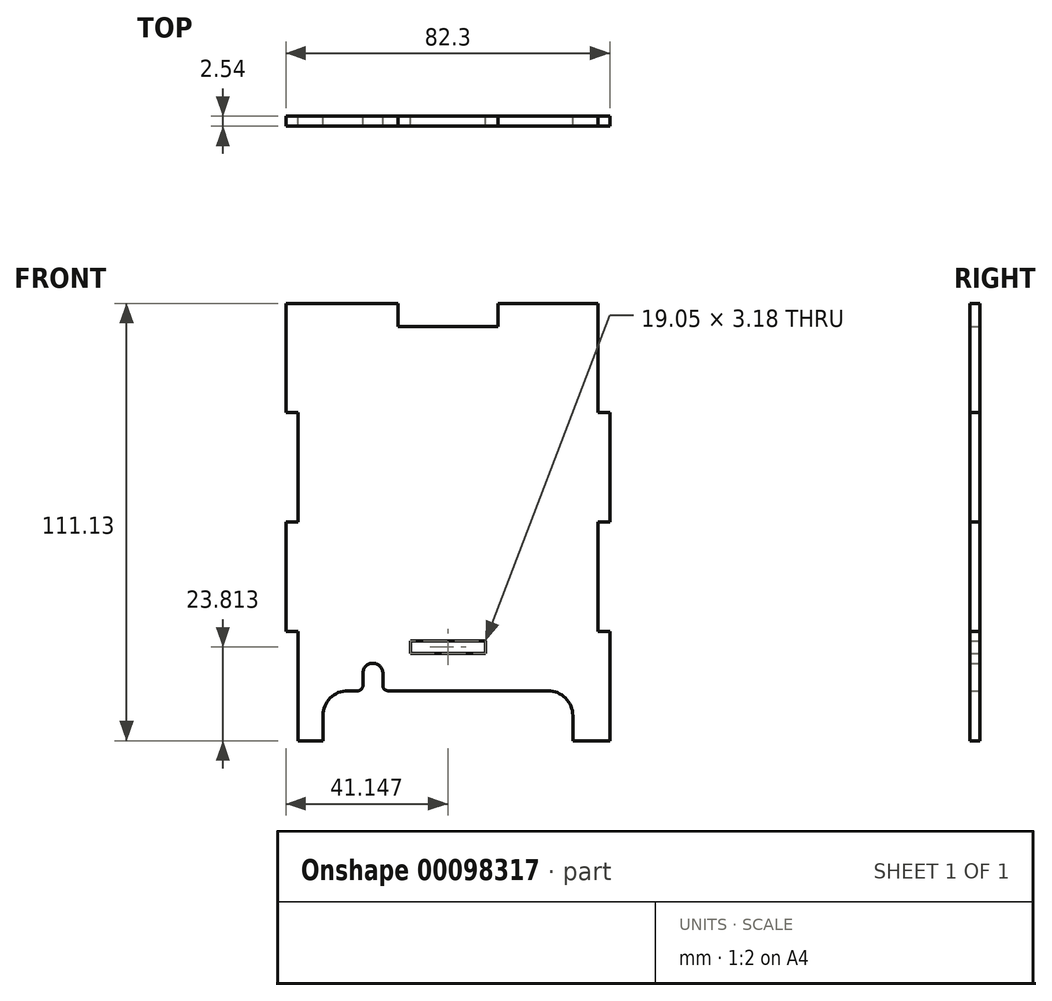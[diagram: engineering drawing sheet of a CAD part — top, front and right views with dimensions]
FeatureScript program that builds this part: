
annotation { "Feature Type Name" : "Feature", "Feature Type Description" : "" }
export const myFeature = defineFeature(function(context is Context, id is Id, definition is map)
    precondition{}
    {
        {
            var Q0;
            Q0=qCreatedBy(makeId("Front.planeOp"),FACE);
            var sketch = newSketch(context, id + "F0", { "sketchPlane" : qUnion([Q0])});
            skLineSegment(sketch, "E0", {"start": v(3.72, 63.77) * mm, "end": v(-8.98, 63.77) * mm});
            skLineSegment(sketch, "E1", {"start": v(-8.98, 63.77) * mm, "end": v(-8.98, 69.62) * mm});
            skLineSegment(sketch, "E2", {"start": v(-8.98, 69.62) * mm, "end": v(-37.43, 69.62) * mm});
            skLineSegment(sketch, "E3", {"start": v(-37.43, 69.62) * mm, "end": v(-37.43, 41.83) * mm});
            skLineSegment(sketch, "E4", {"start": v(-37.43, 41.83) * mm, "end": v(-34.38, 41.83) * mm});
            skLineSegment(sketch, "E5", {"start": v(-34.38, 41.83) * mm, "end": v(-34.38, 14.05) * mm});
            skLineSegment(sketch, "E6", {"start": v(-34.38, 14.05) * mm, "end": v(-37.43, 14.05) * mm});
            skLineSegment(sketch, "E7", {"start": v(-37.43, 14.05) * mm, "end": v(-37.43, -13.73) * mm});
            skLineSegment(sketch, "E8", {"start": v(-37.43, -13.73) * mm, "end": v(-34.38, -13.73) * mm});
            skLineSegment(sketch, "E9", {"start": v(-34.38, -13.73) * mm, "end": v(-34.38, -41.5) * mm});
            skLineSegment(sketch, "E10", {"start": v(-34.38, -41.5) * mm, "end": v(-28.03, -41.5) * mm});
            skLineSegment(sketch, "E11", {"start": v(-28.03, -41.5) * mm, "end": v(-28.03, -35.16) * mm});
            skLineSegment(sketch, "E12", {"start": v(-21.68, -28.8) * mm, "end": v(-19.14, -28.8) * mm});
            skLineSegment(sketch, "E13", {"start": v(35.47, -35.16) * mm, "end": v(35.47, -41.5) * mm});
            skLineSegment(sketch, "E14", {"start": v(35.47, -41.5) * mm, "end": v(44.87, -41.5) * mm});
            skLineSegment(sketch, "E15", {"start": v(44.87, -41.5) * mm, "end": v(44.87, -13.73) * mm});
            skLineSegment(sketch, "E16", {"start": v(44.87, -13.73) * mm, "end": v(41.82, -13.73) * mm});
            skLineSegment(sketch, "E17", {"start": v(41.82, -13.73) * mm, "end": v(41.82, 14.05) * mm});
            skLineSegment(sketch, "E18", {"start": v(41.82, 14.05) * mm, "end": v(44.87, 14.05) * mm});
            skLineSegment(sketch, "E19", {"start": v(44.87, 14.05) * mm, "end": v(44.87, 41.83) * mm});
            skLineSegment(sketch, "E20", {"start": v(44.87, 41.83) * mm, "end": v(41.82, 41.83) * mm});
            skLineSegment(sketch, "E21", {"start": v(41.82, 41.83) * mm, "end": v(41.82, 69.62) * mm});
            skLineSegment(sketch, "E22", {"start": v(41.82, 69.62) * mm, "end": v(16.42, 69.62) * mm});
            skLineSegment(sketch, "E23", {"start": v(16.42, 69.62) * mm, "end": v(16.42, 63.77) * mm});
            skLineSegment(sketch, "E24", {"start": v(16.42, 63.77) * mm, "end": v(3.72, 63.77) * mm});
            skPoint(sketch, "E25.visualSharp", {"position": v(-28.03, -28.8) * mm});
            skArc(sketch, "E25.filletArc", {"start": v(-21.68, -28.8) * mm, "mid": v(-26.17, -30.67) * mm, "end": v(-28.03, -35.16) * mm});
            skPoint(sketch, "E26.visualSharp", {"position": v(35.47, -28.8) * mm});
            skArc(sketch, "E26.filletArc", {"start": v(35.47, -35.16) * mm, "mid": v(33.6, -30.67) * mm, "end": v(29.12, -28.8) * mm});
            skLineSegment(sketch, "E27.bottom", {"start": v(-5.8, -16.1) * mm, "end": v(13.24, -16.1) * mm});
            skLineSegment(sketch, "E27.top", {"start": v(-5.8, -19.28) * mm, "end": v(13.24, -19.28) * mm});
            skLineSegment(sketch, "E27.left", {"start": v(-5.8, -16.1) * mm, "end": v(-5.8, -19.28) * mm});
            skLineSegment(sketch, "E27.right", {"start": v(13.24, -16.1) * mm, "end": v(13.24, -19.28) * mm});
            skLineSegment(sketch, "E28.left", {"start": v(-17.87, -27.54) * mm, "end": v(-17.87, -24.36) * mm});
            skLineSegment(sketch, "E28.right", {"start": v(-12.8, -27.54) * mm, "end": v(-12.8, -24.36) * mm});
            skArc(sketch, "E29", {"start": v(-12.8, -24.36) * mm, "mid": v(-15.33, -21.82) * mm, "end": v(-17.87, -24.36) * mm});
            skLineSegment(sketch, "E30.trimOffspring", {"start": v(-11.52, -28.8) * mm, "end": v(29.12, -28.8) * mm});
            skPoint(sketch, "E31.visualSharp", {"position": v(-17.87, -28.8) * mm});
            skArc(sketch, "E31.filletArc", {"start": v(-19.14, -28.8) * mm, "mid": v(-18.24, -28.44) * mm, "end": v(-17.87, -27.54) * mm});
            skPoint(sketch, "E32.visualSharp", {"position": v(-12.8, -28.8) * mm});
            skArc(sketch, "E32.filletArc", {"start": v(-12.8, -27.54) * mm, "mid": v(-12.42, -28.44) * mm, "end": v(-11.52, -28.8) * mm});
            skSolve(sketch);
        }
        {
            var Q0;
            Q0 = qSketchRegion(id + "F0", true);
            extrude(context, id + "F1", {"entities" : qUnion([Q0]), "depth" : 2.54 * mm});
        }
    });
